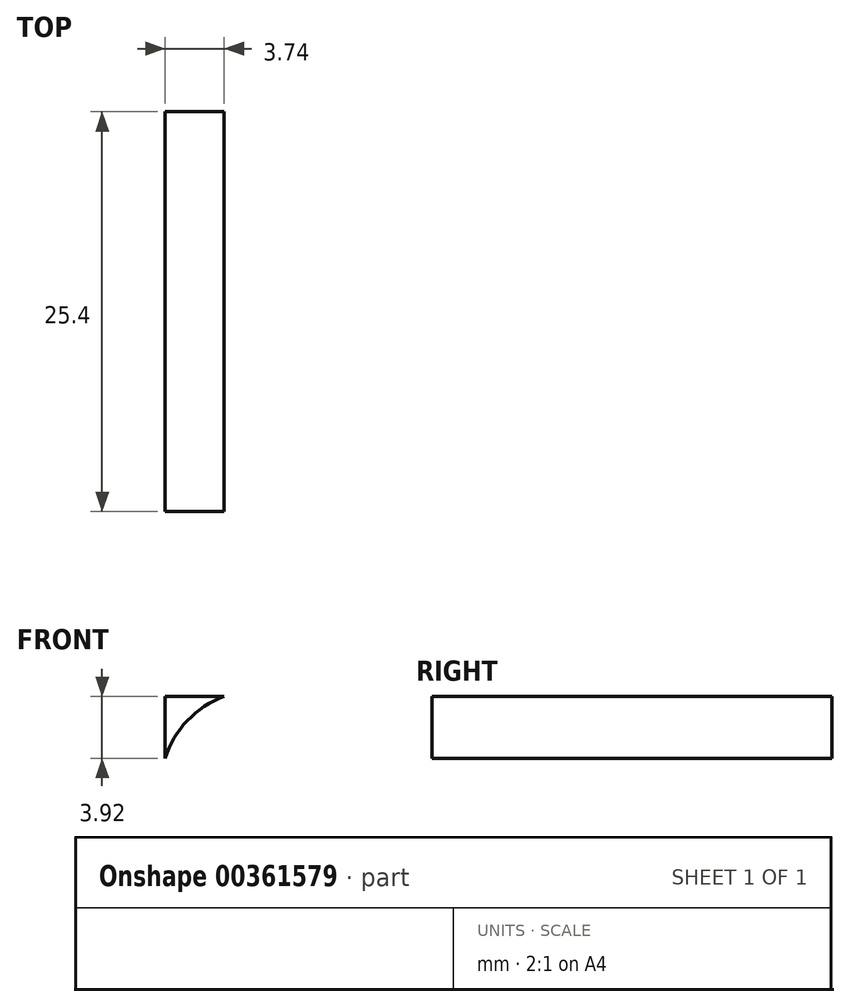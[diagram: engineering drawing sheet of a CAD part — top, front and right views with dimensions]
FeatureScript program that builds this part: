
annotation { "Feature Type Name" : "Feature", "Feature Type Description" : "" }
export const myFeature = defineFeature(function(context is Context, id is Id, definition is map)
    precondition{}
    {
        {
            var Q0;
            Q0=qCreatedBy(makeId("Front.planeOp"),FACE);
            var sketch = newSketch(context, id + "F0", { "sketchPlane" : qUnion([Q0])});
            skLineSegment(sketch, "E0", {"start": v(0, 0) * mm, "end": v(57.15, 0) * mm});
            skLineSegment(sketch, "E1", {"start": v(57.15, 0) * mm, "end": v(57.15, 38.1) * mm});
            skLineSegment(sketch, "E2", {"start": v(57.15, 38.1) * mm, "end": v(0, 38.1) * mm});
            skLineSegment(sketch, "E3", {"start": v(0, 38.1) * mm, "end": v(0, 0) * mm});
            skSolve(sketch);
        }
        {
            var Q0;
            Q0=makeQuery(id+"F0.imprint","IMPRINT",FACE,{"disambiguationData":[TD([[makeQuery(id+"F0.imprint","IMPRINT",EDGE,{"derivedFrom":sQuery(id+"F0.wireOp",EDGE,"E0")}),1.0]])]});
            extrude(context, id + "F1", {"entities" : qUnion([Q0]), "depth" : 25.4 * mm});
        }
        {
            var Q0;
            Q0=makeQuery(id+"F1.opExtrude","CAP_FACE",FACE,{"disambiguationData":[OSD([sQuery(id+"F0.wireOp",EDGE,"E0"),sQuery(id+"F0.wireOp",EDGE,"E1"),sQuery(id+"F0.wireOp",EDGE,"E2"),sQuery(id+"F0.wireOp",EDGE,"E3")])],"isStart":false});
            var sketch = newSketch(context, id + "F2", { "sketchPlane" : qUnion([Q0])});
            skArc(sketch, "E4", {"start": v(38.1, 38.1) * mm, "mid": v(42.3, 23.25) * mm, "end": v(57.15, 19.05) * mm});
            skSolve(sketch);
        }
        {
            var Q0;
            {var subQ0=sQuery(id+"F2.wireOp",EDGE,"E4");Q0=makeQuery(id+"F2.imprint","IMPRINT",FACE,{"disambiguationData":[TD([[makeQuery(id+"F2.imprint","IMPRINT",EDGE,{"derivedFrom":subQ0}),1.0]])]});}
            extrude(context, id + "F3", {"entities" : qUnion([Q0]), "operationType" : NewBodyOperationType.REMOVE, "oppositeDirection" : true, "depth" : 25.4 * mm});
        }
        {
            var Q0;
            Q0=makeQuery(id+"F1.opExtrude","CAP_FACE",FACE,{"disambiguationData":[OSD([sQuery(id+"F0.wireOp",EDGE,"E0"),sQuery(id+"F0.wireOp",EDGE,"E1"),sQuery(id+"F0.wireOp",EDGE,"E2"),sQuery(id+"F0.wireOp",EDGE,"E3")])],"isStart":false});
            var sketch = newSketch(context, id + "F4", { "sketchPlane" : qUnion([Q0])});
            skArc(sketch, "E5", {"start": v(0, 34.18) * mm, "mid": v(1.4, 36.58) * mm, "end": v(3.74, 38.1) * mm});
            skSolve(sketch);
        }
        {
            var Q0;
            {var subQ0=sQuery(id+"F4.wireOp",EDGE,"E5");Q0=makeQuery(id+"F4.imprint","IMPRINT",FACE,{"disambiguationData":[TD([[makeQuery(id+"F4.imprint","IMPRINT",EDGE,{"derivedFrom":subQ0}),1.0]])]});}
            extrude(context, id + "F5", {"entities" : qUnion([Q0]), "operationType" : NewBodyOperationType.REMOVE, "oppositeDirection" : true, "depth" : 25.4 * mm});
        }
    });
